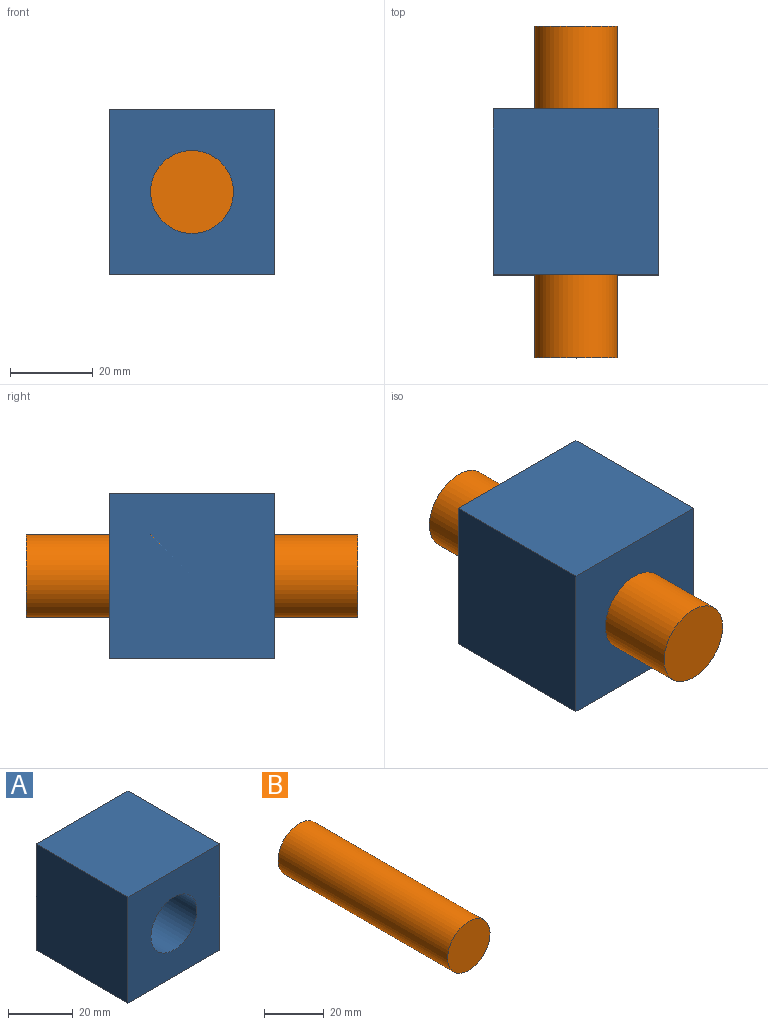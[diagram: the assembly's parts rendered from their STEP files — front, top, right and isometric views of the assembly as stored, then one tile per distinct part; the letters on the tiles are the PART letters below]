
ASSEMBLY  parts=2 mates=1
PART A: 7 faces, bbox 40x40x40 mm
  f0: plane 40x40mm, normal (-1,0,0), area 1600mm2, adj f1,f3,f5,f6
  f1: plane 40x40mm, normal (0,0,-1), area 1600mm2, adj f0,f2,f5,f6
  f2: plane 40x40mm, normal (1,0,0), area 1600mm2, adj f1,f3,f5,f6
  f3: plane 40x40mm, normal (0,0,1), area 1600mm2, adj f0,f2,f5,f6
  f4: cylinder r=10mm len=40mm, axis (0,1,0), area 2513.3mm2, adj f5,f6
  f5: plane 40x40mm, normal (0,-1,0), area 1285.8mm2, adj f0,f1,f2,f3,f4
  f6: plane 40x40mm, normal (0,1,0), area 1285.8mm2, adj f0,f1,f2,f3,f4
PART B: 3 faces, bbox 20x80x20 mm
  f0: cylinder r=10mm len=80mm, axis (0,1,0), area 5026.5mm2, adj f1,f2
  f1: plane 20x20mm, normal (0,-1,0), area 314.2mm2, adj f0
  f2: plane 20x20mm, normal (0,1,0), area 314.2mm2, adj f0
PLACE A t=(-33.78,-16.27,-32.47)mm
PLACE B t=(-13.78,3.73,-12.47)mm
MATE revolute A.f4 <-> B.f0  axis (0,1,0) through (-13.78,-36.27,-12.47)mm
